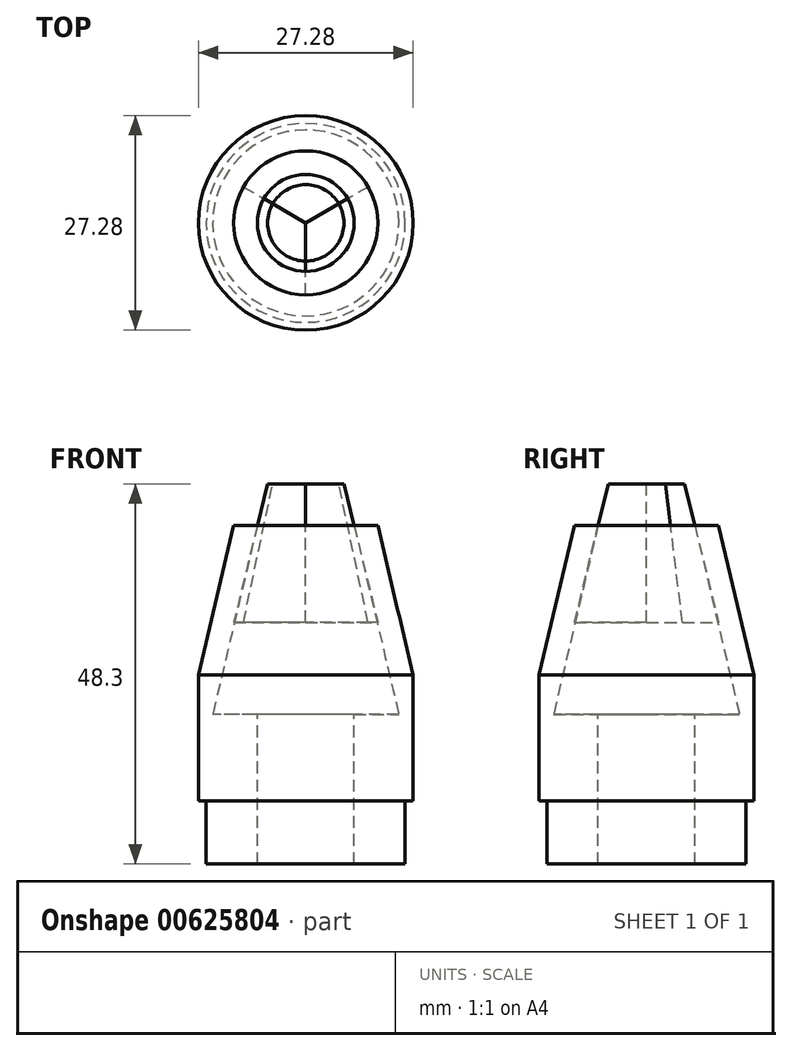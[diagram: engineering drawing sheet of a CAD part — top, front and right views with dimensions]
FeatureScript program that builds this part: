
annotation { "Feature Type Name" : "Feature", "Feature Type Description" : "" }
export const myFeature = defineFeature(function(context is Context, id is Id, definition is map)
    precondition{}
    {
        {
            var Q0;
            Q0=qCreatedBy(makeId("Front.planeOp"),FACE);
            var sketch = newSketch(context, id + "F0", { "sketchPlane" : qUnion([Q0])});
            skLineSegment(sketch, "E0", {"start": v(6.15, 43) * mm, "end": v(9.15, 43) * mm});
            skLineSegment(sketch, "E1", {"start": v(9.15, 43) * mm, "end": v(13.64, 24) * mm});
            skLineSegment(sketch, "E2", {"start": v(13.64, 24) * mm, "end": v(13.64, 8) * mm});
            skLineSegment(sketch, "E3", {"start": v(13.64, 8) * mm, "end": v(12.64, 8) * mm});
            skLineSegment(sketch, "E4", {"start": v(12.64, 8) * mm, "end": v(12.64, 0) * mm});
            skLineSegment(sketch, "E5", {"start": v(12.64, 0) * mm, "end": v(6.14, 0) * mm});
            skLineSegment(sketch, "E6", {"start": v(6.14, 0) * mm, "end": v(6.14, 19) * mm});
            skPoint(sketch, "E7", {"position": v(6.14, 19) * mm});
            skLineSegment(sketch, "E8", {"start": v(6.14, 19) * mm, "end": v(11.82, 19) * mm});
            skLineSegment(sketch, "E9", {"start": v(11.82, 19) * mm, "end": v(6.15, 43) * mm});
            skLineSegment(sketch, "E10", {"start": v(0, 58.14) * mm, "end": v(0, -20.15) * mm, "construction": true});
            skSolve(sketch);
        }
        {
            var Q0;
            Q0=makeQuery(id+"F0.imprint","IMPRINT",FACE,{"disambiguationData":[TD([[makeQuery(id+"F0.imprint","IMPRINT",EDGE,{"derivedFrom":sQuery(id+"F0.wireOp",EDGE,"E0")}),-1.0]])]});
            var Q1;
            Q1=sQuery(id+"F0.wireOp",EDGE,"E10");
            revolve(context, id + "F1", {"entities" : qUnion([Q0]), "axis" : qUnion([Q1]), "revolveType" : RevolveType.FULL});
        }
        {
            var Q0;
            Q0=makeQuery(id+"F1.opRevolve","SWEPT_FACE",FACE,{"disambiguationData":[OSD([sQuery(id+"F0.wireOp",EDGE,"E0")])]});
            var sketch = newSketch(context, id + "F2", { "sketchPlane" : qUnion([Q0])});
            skCircle(sketch, "E11.0", {"center": v(0, 0) * mm, "radius": 6.15 * mm});
            skLineSegment(sketch, "E12", {"start": v(0, 0) * mm, "end": v(5.33, 3.07) * mm});
            skLineSegment(sketch, "E13", {"start": v(0, 0) * mm, "end": v(0, -6.15) * mm});
            skSolve(sketch);
        }
        {
            var Q0;
            Q0=qCreatedBy(makeId("Top.planeOp"),FACE);
            cPlane(context, id + "F3", {"entities" : qUnion([Q0]), "cplaneType" : CPlaneType.OFFSET, "offset" : 30.7 * mm, "width" : 150 * mm, "height" : 150 * mm});
        }
        {
            var Q0;
            Q0=qCreatedBy(id+"F3.planeOp",FACE);
            var sketch = newSketch(context, id + "F4", { "sketchPlane" : qUnion([Q0])});
            skCircle(sketch, "E14.0.0", {"center": v(0, 0) * mm, "radius": 9.15 * mm});
            skLineSegment(sketch, "E15", {"start": v(0, 0) * mm, "end": v(0, -9.15) * mm});
            skLineSegment(sketch, "E16", {"start": v(0, 0) * mm, "end": v(7.92, 4.57) * mm});
            skLineSegment(sketch, "E17.0", {"start": v(0, 0) * mm, "end": v(5.33, 3.07) * mm});
            skSolve(sketch);
        }
        {
            var Q0;
            Q0=qCreatedBy(makeId("Right.planeOp"),FACE);
            var sketch = newSketch(context, id + "F5", { "sketchPlane" : qUnion([Q0])});
            skLineSegment(sketch, "E18", {"start": v(-7.29, 38.19) * mm, "end": v(-4.85, 48.31) * mm, "construction": true});
            skLineSegment(sketch, "E19", {"start": v(-7.29, 38.19) * mm, "end": v(0, 38.19) * mm, "construction": true});
            skSolve(sketch);
        }
        {
            var Q0;
            Q0=qCreatedBy(id+"F3.planeOp",FACE);
            cPlane(context, id + "F6", {"entities" : qUnion([Q0]), "cplaneType" : CPlaneType.OFFSET, "offset" : 17.6 * mm, "width" : 150 * mm, "height" : 150 * mm});
        }
        {
            var Q0;
            Q0=qCreatedBy(id+"F6.planeOp",FACE);
            var sketch = newSketch(context, id + "F7", { "sketchPlane" : qUnion([Q0])});
            skPoint(sketch, "E20.0", {"position": v(0, -4.85) * mm});
            skCircle(sketch, "E21", {"center": v(0, 0) * mm, "radius": 4.85 * mm});
            skLineSegment(sketch, "E22", {"start": v(0, -4.85) * mm, "end": v(0, 0) * mm});
            skLineSegment(sketch, "E23.0", {"start": v(0, 0) * mm, "end": v(5.33, 3.07) * mm});
            skLineSegment(sketch, "E24", {"start": v(0, 0) * mm, "end": v(4.2, 2.42) * mm});
            skSolve(sketch);
        }
        {
            var Q1;
            {var subQ0=sQuery(id+"F4.wireOp",EDGE,"E15");Q1=makeQuery(id+"F4.imprint","IMPRINT",FACE,{"disambiguationData":[TD([[makeQuery(id+"F4.imprint","IMPRINT",EDGE,{"derivedFrom":subQ0}),1.0]])]});}
            var Q2;
            {var subQ0=sQuery(id+"F7.wireOp",EDGE,"E22");Q2=makeQuery(id+"F7.imprint","IMPRINT",FACE,{"disambiguationData":[TD([[makeQuery(id+"F7.imprint","IMPRINT",EDGE,{"derivedFrom":subQ0}),-1.0]])]});}
            var Q3;
            Q3=sQuery(id+"F4.wireOp",VERTEX,"E16.end");
            var Q4;
            Q4=sQuery(id+"F7.wireOp",VERTEX,"E24.end");
            loft(context, id + "F8", {"sheetProfilesArray" : [{ "sheetProfileEntities" : qUnion([Q1]) }, { "sheetProfileEntities" : qUnion([Q2]) }], "matchConnections" : true, "connections" : [{ "connectionEntities" : qUnion([Q3, Q4]), "connectionEdgeQueries" : qUnion([]), "connectionEdgeParameters" : [] }]});
        }
        {
            var Q0;
            {var subQ0=sQuery(id+"F7.wireOp",EDGE,"E22");var subQ3=sQuery(id+"F4.wireOp",EDGE,"E15");Q0=makeQuery(id+"F8.opLoft","SWEPT_BODY",BODY,{"disambiguationData":[OSD([makeQuery(id+"F4.imprint","IMPRINT",FACE,{"disambiguationData":[TD([[makeQuery(id+"F4.imprint","IMPRINT",EDGE,{"derivedFrom":subQ3}),1.0]])]}),makeQuery(id+"F7.imprint","IMPRINT",FACE,{"disambiguationData":[TD([[makeQuery(id+"F7.imprint","IMPRINT",EDGE,{"derivedFrom":subQ0}),-1.0]])]})])]});}
            var Q1;
            Q1=makeQuery(id+"F1.opRevolve","SWEPT_EDGE",EDGE,{"disambiguationData":[OSD([sQuery(id+"F0.wireOp",EDGE,"E0"),sQuery(id+"F0.wireOp",EDGE,"E1")])]});
            circularPattern(context, id + "F9", {"entities" : qUnion([Q0]), "axis" : qUnion([Q1]), "angle" : 360 * degree, "instanceCount" : 3, "equalSpace" : true});
        }
    });
